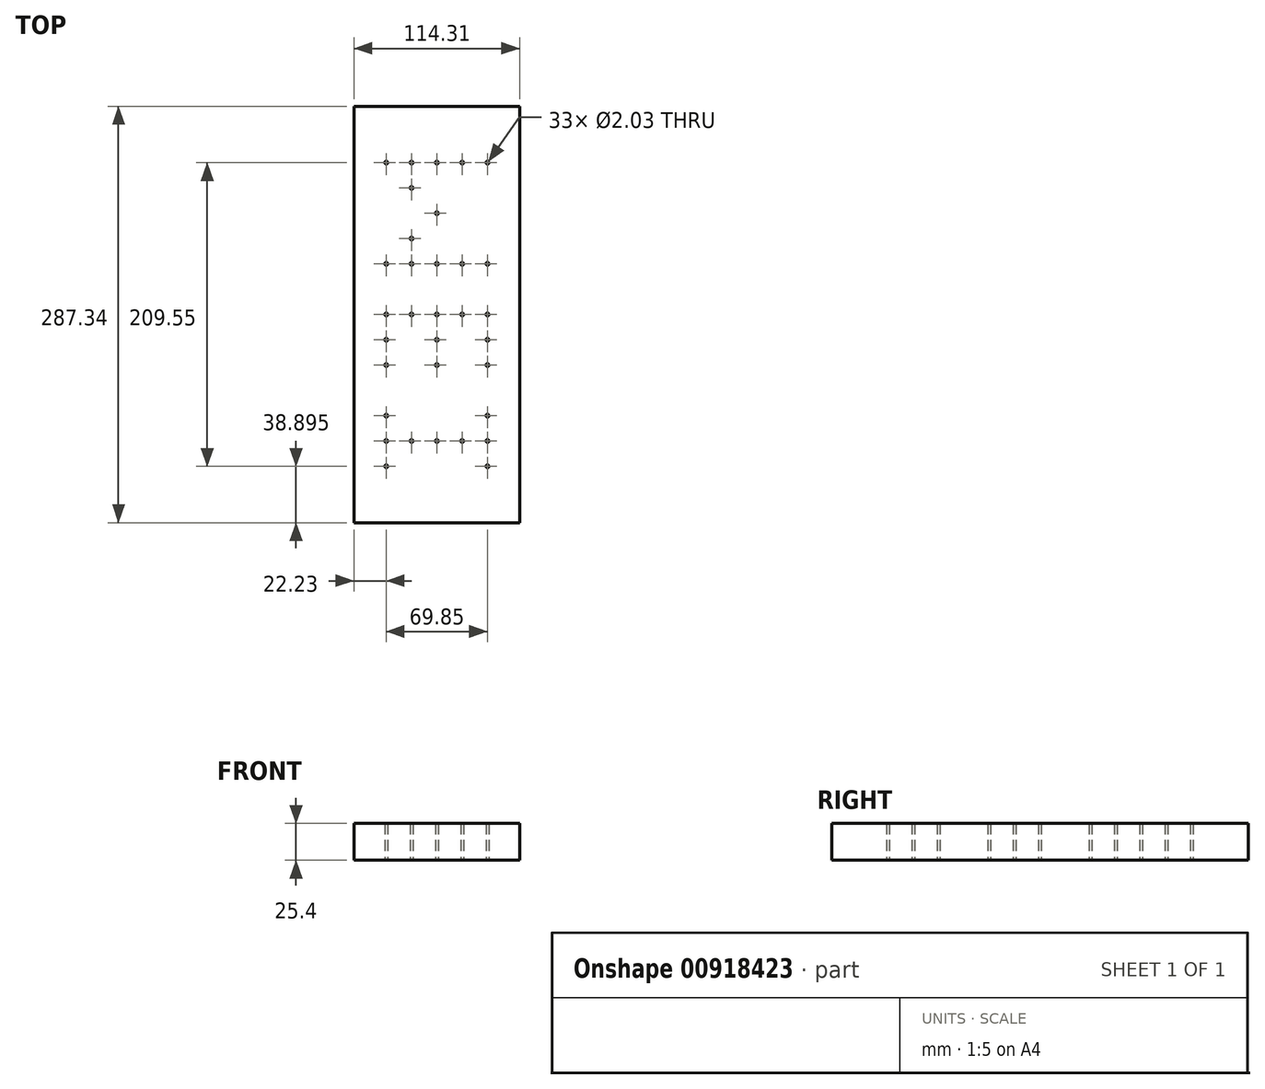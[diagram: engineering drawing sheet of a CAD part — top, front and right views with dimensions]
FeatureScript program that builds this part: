
annotation { "Feature Type Name" : "Feature", "Feature Type Description" : "" }
export const myFeature = defineFeature(function(context is Context, id is Id, definition is map)
    precondition{}
    {
        {
            var Q0;
            Q0=qCreatedBy(makeId("Top.planeOp"),FACE);
            var sketch = newSketch(context, id + "F0", { "sketchPlane" : qUnion([Q0])});
            skLineSegment(sketch, "E0", {"start": v(0, 152.31) * mm, "end": v(-69.85, 152.31) * mm});
            skLineSegment(sketch, "E1", {"start": v(0, 82.46) * mm, "end": v(-69.85, 82.46) * mm});
            skLineSegment(sketch, "E2", {"start": v(-69.85, 152.31) * mm, "end": v(-34.93, 117.39) * mm});
            skLineSegment(sketch, "E3", {"start": v(-34.92, 117.39) * mm, "end": v(-69.85, 82.46) * mm});
            skCircle(sketch, "E4", {"center": v(0, 152.31) * mm, "radius": 1.02 * mm});
            skCircle(sketch, "E5", {"center": v(-69.85, 152.31) * mm, "radius": 1.02 * mm});
            skCircle(sketch, "E6", {"center": v(-34.93, 117.39) * mm, "radius": 1.02 * mm});
            skCircle(sketch, "E7", {"center": v(0, 82.46) * mm, "radius": 1.02 * mm});
            skCircle(sketch, "E8", {"center": v(-69.85, 82.46) * mm, "radius": 1.02 * mm});
            skCircle(sketch, "E9", {"center": v(-34.93, 152.31) * mm, "radius": 1.02 * mm});
            skCircle(sketch, "E10", {"center": v(-17.46, 152.31) * mm, "radius": 1.02 * mm});
            skCircle(sketch, "E11", {"center": v(-52.39, 152.31) * mm, "radius": 1.02 * mm});
            skCircle(sketch, "E12", {"center": v(-34.93, 82.46) * mm, "radius": 1.02 * mm});
            skCircle(sketch, "E13", {"center": v(-52.39, 82.46) * mm, "radius": 1.02 * mm});
            skCircle(sketch, "E14", {"center": v(-17.46, 82.46) * mm, "radius": 1.02 * mm});
            skLineSegment(sketch, "E15", {"start": v(0, 47.54) * mm, "end": v(-69.85, 47.54) * mm});
            skLineSegment(sketch, "E16", {"start": v(-69.85, 47.54) * mm, "end": v(-69.85, 12.61) * mm});
            skLineSegment(sketch, "E17", {"start": v(-34.93, 47.54) * mm, "end": v(-34.93, 12.61) * mm});
            skLineSegment(sketch, "E18", {"start": v(0, 47.54) * mm, "end": v(0, 12.61) * mm});
            skLineSegment(sketch, "E19", {"start": v(0, -39.77) * mm, "end": v(-69.85, -39.77) * mm});
            skLineSegment(sketch, "E20", {"start": v(0, -39.77) * mm, "end": v(0, -22.31) * mm});
            skLineSegment(sketch, "E21", {"start": v(-69.85, -39.77) * mm, "end": v(-69.85, -22.31) * mm});
            skLineSegment(sketch, "E22.MirrorCS", {"start": v(0, -39.77) * mm, "end": v(0, -57.24) * mm});
            skLineSegment(sketch, "E23.MirrorCS", {"start": v(-69.85, -39.77) * mm, "end": v(-69.85, -57.24) * mm});
            skCircle(sketch, "E24", {"center": v(-52.39, 99.93) * mm, "radius": 1.02 * mm});
            skCircle(sketch, "E25", {"center": v(-69.85, 30.08) * mm, "radius": 1.02 * mm});
            skCircle(sketch, "E26", {"center": v(-34.93, 30.08) * mm, "radius": 1.02 * mm});
            skCircle(sketch, "E27", {"center": v(0, 47.54) * mm, "radius": 1.02 * mm});
            skCircle(sketch, "E28", {"center": v(0, 12.61) * mm, "radius": 1.02 * mm});
            skCircle(sketch, "E29", {"center": v(-34.93, 47.54) * mm, "radius": 1.02 * mm});
            skCircle(sketch, "E30", {"center": v(-34.92, 12.61) * mm, "radius": 1.02 * mm});
            skCircle(sketch, "E31", {"center": v(-69.85, 47.54) * mm, "radius": 1.02 * mm});
            skCircle(sketch, "E32", {"center": v(-69.85, 12.61) * mm, "radius": 1.02 * mm});
            skCircle(sketch, "E33", {"center": v(-69.85, -22.31) * mm, "radius": 1.02 * mm});
            skCircle(sketch, "E34", {"center": v(-69.85, -39.77) * mm, "radius": 1.02 * mm});
            skCircle(sketch, "E35", {"center": v(-69.85, -57.24) * mm, "radius": 1.02 * mm});
            skCircle(sketch, "E36", {"center": v(-34.93, -39.77) * mm, "radius": 1.02 * mm});
            skCircle(sketch, "E37", {"center": v(-17.46, 47.54) * mm, "radius": 1.02 * mm});
            skCircle(sketch, "E38", {"center": v(-52.39, 47.54) * mm, "radius": 1.02 * mm});
            skCircle(sketch, "E39", {"center": v(-17.46, -39.77) * mm, "radius": 1.02 * mm});
            skCircle(sketch, "E40", {"center": v(-52.39, -39.77) * mm, "radius": 1.02 * mm});
            skCircle(sketch, "E41", {"center": v(0, -22.31) * mm, "radius": 1.02 * mm});
            skCircle(sketch, "E42", {"center": v(0, -39.77) * mm, "radius": 1.02 * mm});
            skCircle(sketch, "E43", {"center": v(0, -57.24) * mm, "radius": 1.02 * mm});
            skCircle(sketch, "E44", {"center": v(0, 30.08) * mm, "radius": 1.02 * mm});
            skCircle(sketch, "E45", {"center": v(-52.39, 134.85) * mm, "radius": 1.02 * mm});
            skLineSegment(sketch, "E46", {"start": v(-92.08, 191.2) * mm, "end": v(-92.07, -96.13) * mm});
            skLineSegment(sketch, "E47", {"start": v(22.23, -96.13) * mm, "end": v(-92.07, -96.13) * mm});
            skLineSegment(sketch, "E48", {"start": v(22.22, 191.2) * mm, "end": v(-92.08, 191.2) * mm});
            skLineSegment(sketch, "E49", {"start": v(22.22, 191.2) * mm, "end": v(22.23, -96.13) * mm});
            skSolve(sketch);
        }
        {
            var Q0;
            Q0=makeQuery(id+"F0.imprint","IMPRINT",FACE,{"disambiguationData":[TD([[makeQuery(id+"F0.imprint","IMPRINT",EDGE,{"derivedFrom":sQuery(id+"F0.wireOp",EDGE,"E4")}),-1.0]])]});
            extrude(context, id + "F1", {"entities" : qUnion([Q0]), "depth" : 25.4 * mm, "offsetDistance" : 25.4 * mm});
        }
    });
